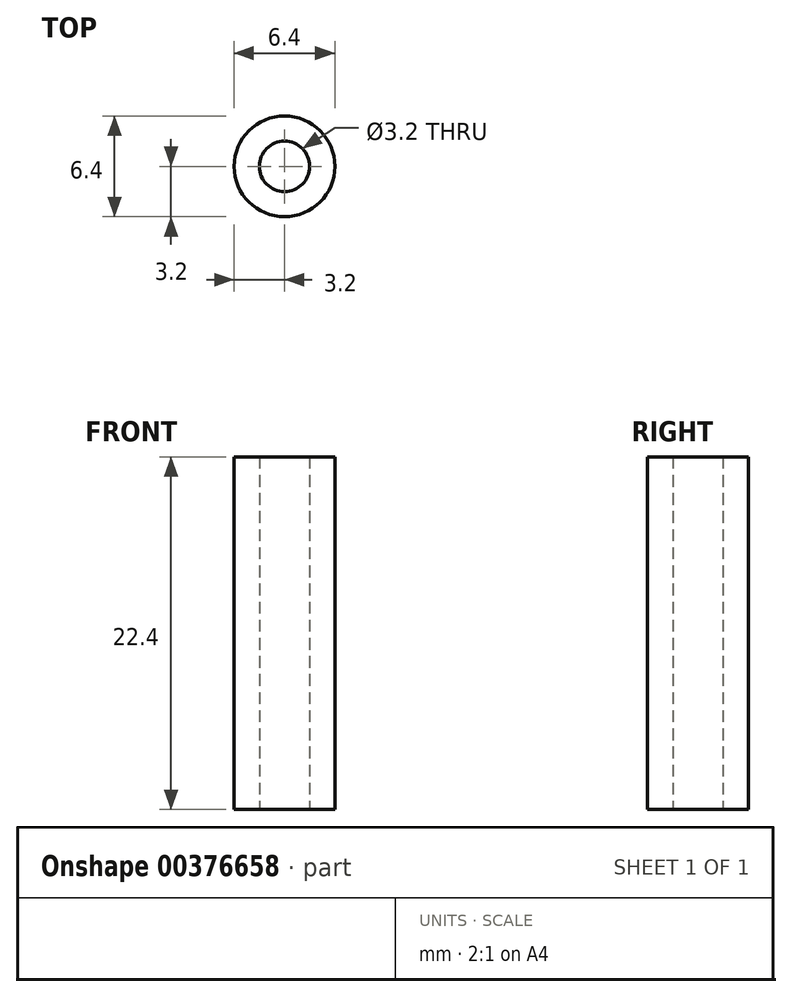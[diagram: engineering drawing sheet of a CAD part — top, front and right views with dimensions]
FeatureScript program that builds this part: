
annotation { "Feature Type Name" : "Feature", "Feature Type Description" : "" }
export const myFeature = defineFeature(function(context is Context, id is Id, definition is map)
    precondition{}
    {
        {
            var Q0;
            Q0=qCreatedBy(makeId("Top.planeOp"),FACE);
            var sketch = newSketch(context, id + "F0", { "sketchPlane" : qUnion([Q0])});
            skCircle(sketch, "E0", {"center": v(0, 0) * mm, "radius": 1.6 * mm});
            skCircle(sketch, "E1", {"center": v(0, 0) * mm, "radius": 3.2 * mm});
            skSolve(sketch);
        }
        {
            var Q0;
            Q0=makeQuery(id+"F0.imprint","IMPRINT",FACE,{"disambiguationData":[TD([[makeQuery(id+"F0.imprint","IMPRINT",EDGE,{"derivedFrom":sQuery(id+"F0.wireOp",EDGE,"E0")}),-1.0]])]});
            extrude(context, id + "F1", {"entities" : qUnion([Q0]), "depth" : 22.4 * mm, "offsetDistance" : 25 * mm});
        }
    });
